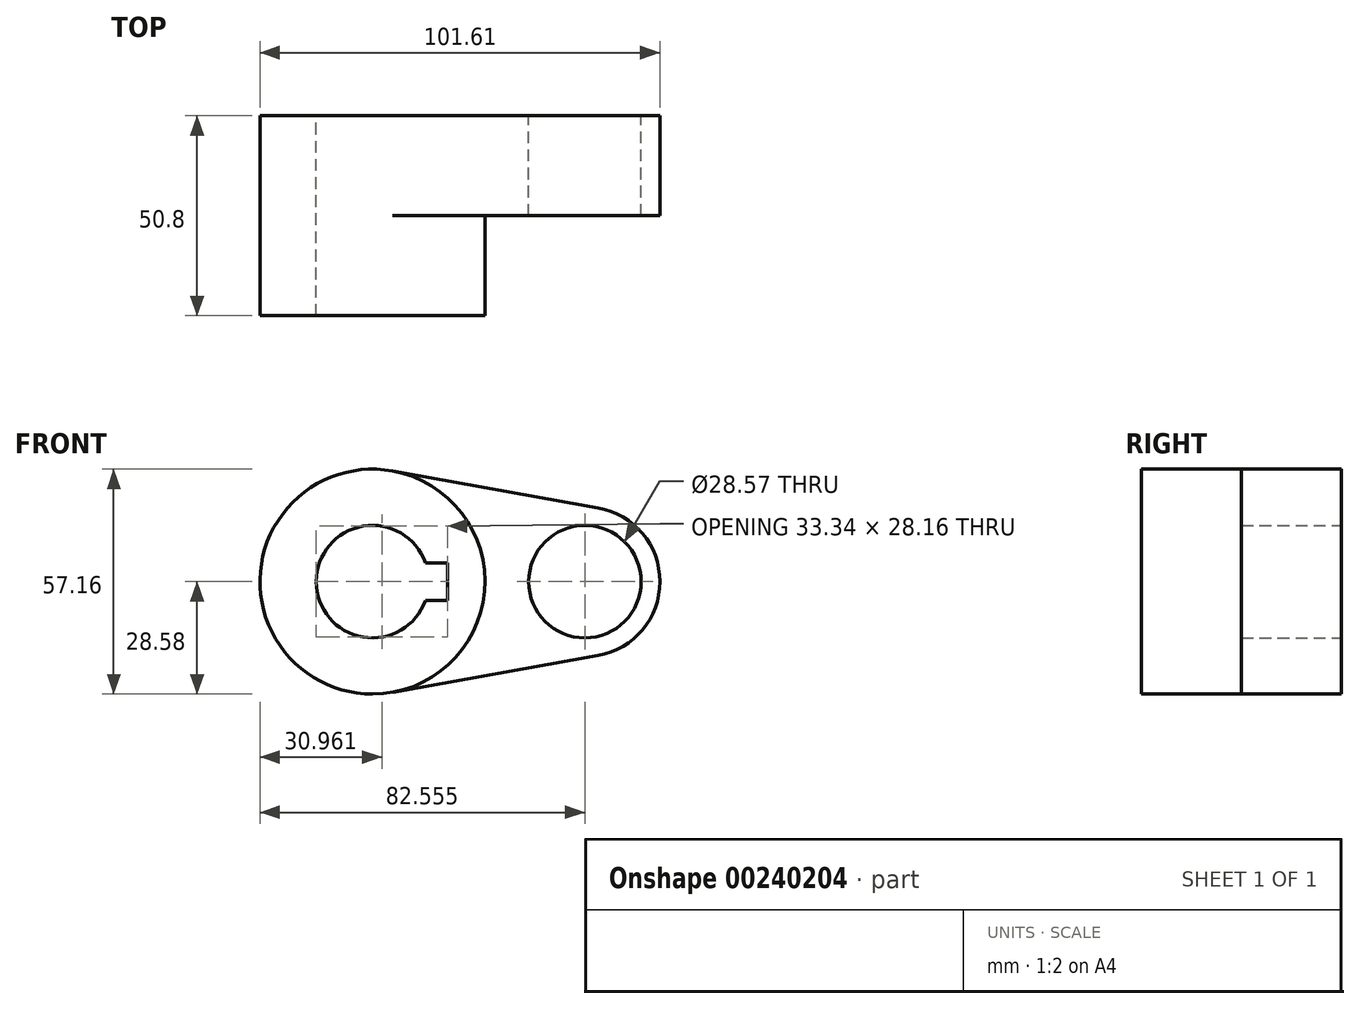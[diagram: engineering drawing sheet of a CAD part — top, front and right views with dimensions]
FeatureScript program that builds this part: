
annotation { "Feature Type Name" : "Feature", "Feature Type Description" : "" }
export const myFeature = defineFeature(function(context is Context, id is Id, definition is map)
    precondition{}
    {
        {
            var Q0;
            Q0=qCreatedBy(makeId("Front.planeOp"),FACE);
            var sketch = newSketch(context, id + "F0", { "sketchPlane" : qUnion([Q0])});
            skCircle(sketch, "E0", {"center": v(0, 0) * mm, "radius": 28.58 * mm});
            skCircle(sketch, "E1", {"center": v(53.98, 0) * mm, "radius": 19.05 * mm});
            skLineSegment(sketch, "E2", {"start": v(5.04, 28.13) * mm, "end": v(57.34, 18.75) * mm});
            skLineSegment(sketch, "E3", {"start": v(57.34, -18.75) * mm, "end": v(5.04, -28.13) * mm});
            skCircle(sketch, "E4", {"center": v(0, 0) * mm, "radius": 14.29 * mm});
            skCircle(sketch, "E5", {"center": v(53.98, 0) * mm, "radius": 14.29 * mm});
            skLineSegment(sketch, "E6.bottom", {"start": v(19.05, 4.76) * mm, "end": v(-19.05, 4.76) * mm});
            skLineSegment(sketch, "E6.top", {"start": v(19.05, -4.76) * mm, "end": v(-19.05, -4.76) * mm});
            skLineSegment(sketch, "E6.left", {"start": v(19.05, 4.76) * mm, "end": v(19.05, -4.76) * mm});
            skLineSegment(sketch, "E6.right", {"start": v(-19.05, 4.76) * mm, "end": v(-19.05, -4.76) * mm});
            skSolve(sketch);
        }
        {
            var Q0;
            {var subQ5=sQuery(id+"F0.wireOp",EDGE,"E6.right");Q0=makeQuery(id+"F0.imprint","IMPRINT",FACE,{"disambiguationData":[TD([[makeQuery(id+"F0.imprint","IMPRINT",EDGE,{"derivedFrom":subQ5}),1.0]])]});}
            var Q1;
            {var subQ11=sQuery(id+"F0.wireOp",EDGE,"E6.left");Q1=makeQuery(id+"F0.imprint","IMPRINT",FACE,{"disambiguationData":[TD([[makeQuery(id+"F0.imprint","IMPRINT",EDGE,{"derivedFrom":subQ11}),1.0]])]});}
            var Q2;
            Q2=makeQuery(id+"F0.imprint","IMPRINT",FACE,{"disambiguationData":[TD([[makeQuery(id+"F0.imprint","IMPRINT",EDGE,{"derivedFrom":sQuery(id+"F0.wireOp",EDGE,"E5")}),-1.0]])]});
            var Q3;
            {var subQ0=sQuery(id+"F0.wireOp",EDGE,"E2");Q3=makeQuery(id+"F0.imprint","IMPRINT",FACE,{"disambiguationData":[TD([[makeQuery(id+"F0.imprint","IMPRINT",EDGE,{"derivedFrom":subQ0}),-1.0]])]});}
            extrude(context, id + "F1", {"entities" : qUnion([Q0, Q1, Q2, Q3]), "depth" : 25.4 * mm});
        }
        {
            var Q0;
            {var subQ11=sQuery(id+"F0.wireOp",EDGE,"E6.left");Q0=makeQuery(id+"F0.imprint","IMPRINT",FACE,{"disambiguationData":[TD([[makeQuery(id+"F0.imprint","IMPRINT",EDGE,{"derivedFrom":subQ11}),1.0]])]});}
            var Q1;
            {var subQ5=sQuery(id+"F0.wireOp",EDGE,"E6.right");Q1=makeQuery(id+"F0.imprint","IMPRINT",FACE,{"disambiguationData":[TD([[makeQuery(id+"F0.imprint","IMPRINT",EDGE,{"derivedFrom":subQ5}),1.0]])]});}
            extrude(context, id + "F2", {"entities" : qUnion([Q0, Q1]), "operationType" : NewBodyOperationType.ADD, "depth" : 50.8 * mm});
        }
    });
